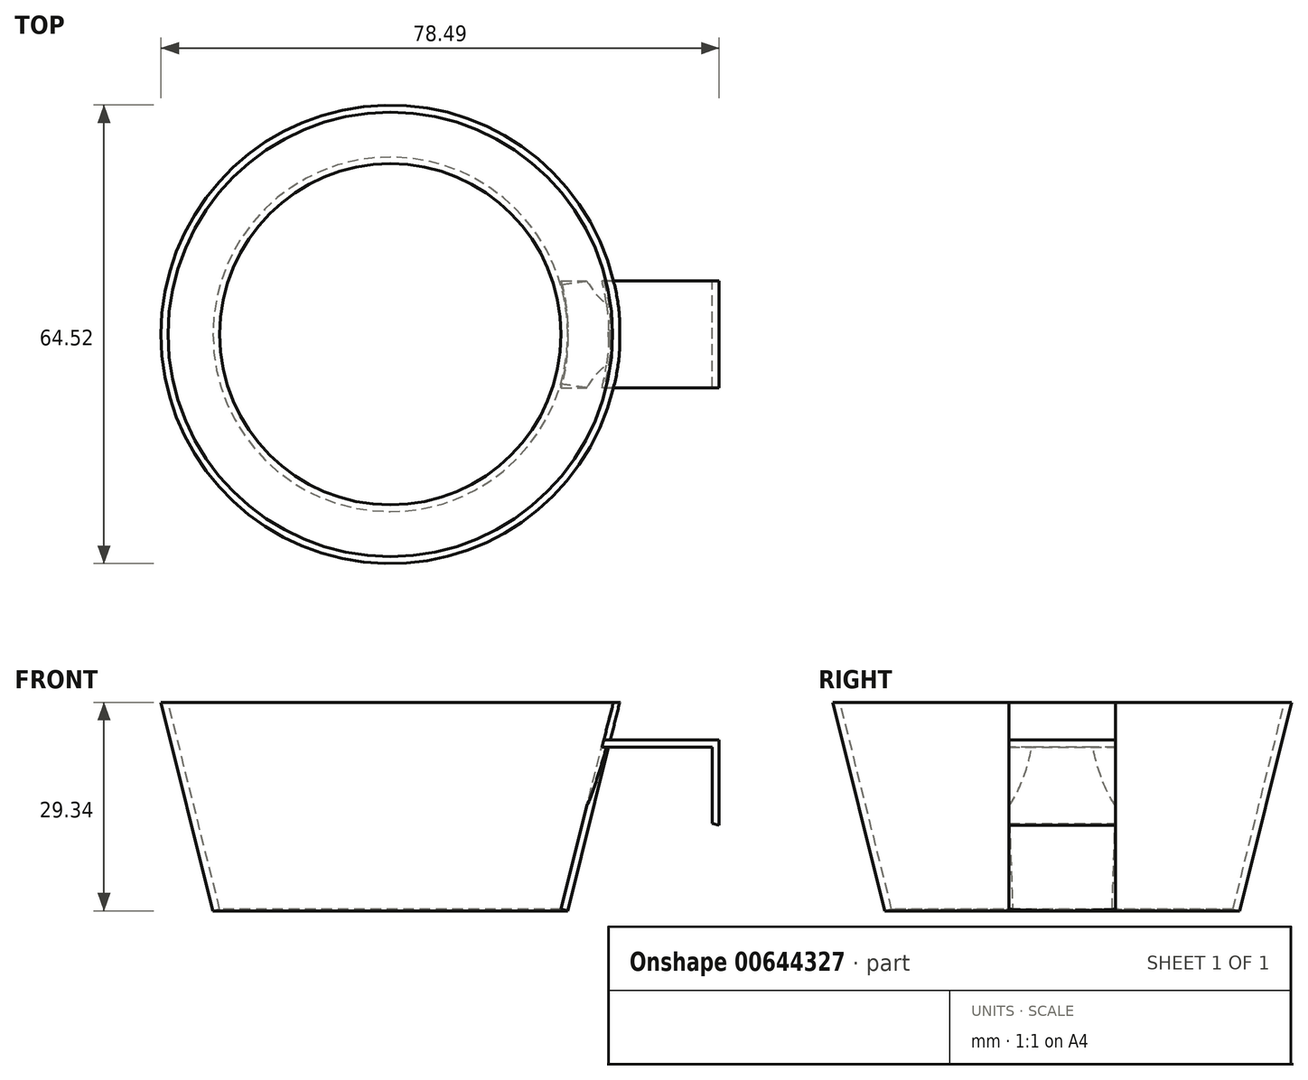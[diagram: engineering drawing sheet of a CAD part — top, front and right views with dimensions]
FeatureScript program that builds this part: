
annotation { "Feature Type Name" : "Feature", "Feature Type Description" : "" }
export const myFeature = defineFeature(function(context is Context, id is Id, definition is map)
    precondition{}
    {
        {
            var Q0;
            Q0=qCreatedBy(makeId("Front.planeOp"),FACE);
            var sketch = newSketch(context, id + "F0", { "sketchPlane" : qUnion([Q0])});
            skLineSegment(sketch, "E0", {"start": v(32.26, 17.31) * mm, "end": v(24.94, -12.03) * mm});
            skLineSegment(sketch, "E1", {"start": v(24.94, -12.03) * mm, "end": v(24, -11.8) * mm});
            skLineSegment(sketch, "E2", {"start": v(24, -11.8) * mm, "end": v(31.26, 17.31) * mm});
            skLineSegment(sketch, "E3", {"start": v(31.26, 17.31) * mm, "end": v(32.26, 17.31) * mm});
            skLineSegment(sketch, "E4", {"start": v(0, 16.67) * mm, "end": v(0, 0) * mm});
            skLineSegment(sketch, "E5", {"start": v(30.93, 12) * mm, "end": v(46.23, 12) * mm});
            skLineSegment(sketch, "E6", {"start": v(46.23, 12) * mm, "end": v(46.23, 0) * mm});
            skLineSegment(sketch, "E7", {"start": v(46.23, 0) * mm, "end": v(45.26, 0.24) * mm});
            skLineSegment(sketch, "E8", {"start": v(45.26, 0.24) * mm, "end": v(45.26, 11) * mm});
            skLineSegment(sketch, "E9", {"start": v(45.26, 11) * mm, "end": v(30.68, 11) * mm});
            skSolve(sketch);
        }
        {
            var Q0;
            Q0=makeQuery(id+"F0.imprint","IMPRINT",FACE,{"disambiguationData":[TD([[makeQuery(id+"F0.imprint","IMPRINT",EDGE,{"derivedFrom":sQuery(id+"F0.wireOp",EDGE,"E0")}),-1.0]])]});
            var Q1;
            Q1=sQuery(id+"F0.wireOp",EDGE,"E4");
            revolve(context, id + "F1", {"entities" : qUnion([Q0]), "axis" : qUnion([Q1]), "revolveType" : RevolveType.FULL});
        }
        {
            var Q0;
            {var subQ0=sQuery(id+"F0.wireOp",EDGE,"E5");Q0=makeQuery(id+"F0.imprint","IMPRINT",FACE,{"disambiguationData":[TD([[makeQuery(id+"F0.imprint","IMPRINT",EDGE,{"derivedFrom":subQ0}),-1.0]])]});}
            var Q1;
            {var subQ0=sQuery(id+"F0.wireOp",EDGE,"E1");Q1=makeQuery(id+"F0.imprint","IMPRINT",FACE,{"disambiguationData":[TD([[makeQuery(id+"F0.imprint","IMPRINT",EDGE,{"derivedFrom":subQ0}),-1.0]])]});}
            extrude(context, id + "F2", {"entities" : qUnion([Q0, Q1]), "operationType" : NewBodyOperationType.ADD, "endBound" : BoundingType.SYMMETRIC, "depth" : 15 * mm, "offsetDistance" : 25 * mm});
        }
        {
            var Q0;
            {var subQ0=sQuery(id+"F0.wireOp",EDGE,"E0");Q0=makeQuery(id+"F2.opExtrude","CAP_EDGE",EDGE,{"disambiguationData":[OSD([subQ0]),TDD([makeQuery(id+"F0.imprint","IMPRINT",EDGE,{"disambiguationData":[TD([[makeQuery(id+"F0.imprint","INTERSECT",VERTEX,{"derivedFrom":[subQ0,sQuery(id+"F0.wireOp",EDGE,"E1")]}),1.0]])],"derivedFrom":subQ0})])],"isStart":true});}
            fillet(context, id + "F3", {"entities" : qUnion([Q0]), "radius" : 27 * mm, "tangentPropagation" : true, "allowEdgeOverflow" : false});
        }
        {
            var Q0;
            {var subQ0=sQuery(id+"F0.wireOp",EDGE,"E0");Q0=makeQuery(id+"F2.opExtrude","CAP_EDGE",EDGE,{"disambiguationData":[OSD([subQ0]),TDD([makeQuery(id+"F0.imprint","IMPRINT",EDGE,{"disambiguationData":[TD([[makeQuery(id+"F0.imprint","INTERSECT",VERTEX,{"derivedFrom":[subQ0,sQuery(id+"F0.wireOp",EDGE,"E1")]}),1.0]])],"derivedFrom":subQ0})])],"isStart":false});}
            fillet(context, id + "F4", {"entities" : qUnion([Q0]), "radius" : 27 * mm, "tangentPropagation" : true, "allowEdgeOverflow" : false});
        }
        {
            var Q0;
            {var subQ0=sQuery(id+"F0.wireOp",EDGE,"E0");Q0=makeQuery(id+"F2.opExtrude","CAP_EDGE",EDGE,{"disambiguationData":[OSD([subQ0]),TDD([makeQuery(id+"F0.imprint","IMPRINT",EDGE,{"disambiguationData":[TD([[makeQuery(id+"F0.imprint","INTERSECT",VERTEX,{"derivedFrom":[subQ0,sQuery(id+"F0.wireOp",EDGE,"E3")]}),-1.0]])],"derivedFrom":subQ0})])],"isStart":true});}
            var Q1;
            {var subQ0=sQuery(id+"F0.wireOp",EDGE,"E0");Q1=makeQuery(id+"F2.opExtrude","CAP_EDGE",EDGE,{"disambiguationData":[OSD([subQ0]),TDD([makeQuery(id+"F0.imprint","IMPRINT",EDGE,{"disambiguationData":[TD([[makeQuery(id+"F0.imprint","INTERSECT",VERTEX,{"derivedFrom":[subQ0,sQuery(id+"F0.wireOp",EDGE,"E3")]}),-1.0]])],"derivedFrom":subQ0})])],"isStart":false});}
            fillet(context, id + "F5", {"entities" : qUnion([Q0, Q1]), "radius" : 27 * mm, "tangentPropagation" : true, "allowEdgeOverflow" : false});
        }
    });
